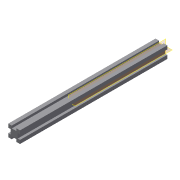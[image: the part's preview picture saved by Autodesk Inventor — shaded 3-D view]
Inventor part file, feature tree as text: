
AUTODESK INVENTOR PART (.ipt)
format: ipt  version: 2019.4 (Build 234330000, 330)  size: 107,520 bytes
history: native  units: mm
features: plane x2, extrude x1, sketch x1
ambient origin geometry x8: Origin, YZ Plane, XZ Plane, XY Plane, X Axis, Y Axis, Z Axis, Center Point
bodies: Solid1 (feature_tree)
feature tree (4):
  extrude  "Extrusion1"  Depth=20.0mm
  plane  "Work Plane1"
  plane  "Work Plane2"
  sketch  "Sketch1"  dims[d0=20.0mm d1=20.0mm d2=8.0mm d3=8.0mm d4=8.0mm d5=8.0mm d6=8.0mm d7=8.0mm d8=8.0mm d9=8.0mm d10=250.0mm d11=0.0mm]
